# Revit family: PRD_AR_DrnngTps_DrainValve_ACXX2009
name_source: partatom
category: Plumbing Fixtures
units: mm (PartAtom-declared; Revit-internal decimal feet)

## family parameters
Always vertical = Yes
Cut with Voids When Loaded = No
OmniClass Number = 23.65.55.14.21
OmniClass Title = Non-Return Valves for Liquid Services
Part Type = Normal
Room Calculation Point = No
Round Connector Dimension = Use Diameter
Shared = No
Work Plane-Based = No

## types (1)
- ACXX2009
    AssetType = Fixed
    BIMObjectName = PRD_AR_DrainingTaps_DrainValve_ACXX2009
    BodyMaterial = PRD_AR_ChromatedBrass
    Category = Pr_65_54_95_27, Draining taps
    CloseOffRating = 0.0 Pa
    Default Elevation = 0 mm  [stored 0 ft]
    Description = Drain valve for automatic shower hose drainage for installation on wall-mounted mixers with hand shower connection, G 1/2 x G 1/2 A, polished chromium-plated brass.
    DurationUnit = year
    Features = for installation on wall-mounted mixers with hand shower connection
    FlowCoefficient = 0
    IfcExportAs = IfcValveType
    IfcExportType = USERDEFINED
    Manufacturer = KWC Group AG
    ManufacturerName = KWC Group AG
    ManufacturerURL = www.kwc.com
    Model = ACXX2009
    ModelNumber = 2030068123
    ModelReference = ACXX2009
    NBSDescription = Draining taps
    NBSReference = 90-10-90/374
    Name = Drain valve for automatic shower hose drainage ACXX2009
    NominalDepth = 0 mm  [stored 0 ft]
    NominalHeight = 0 mm  [stored 0 ft]
    NominalWidth = 0 mm  [stored 0 ft]
    ProductInformation = http://pim.kwc.com
    Quantity = 1
    QuantityUom = piece
    Size = 0.000000000000
    Status = New
    TailorMade = no
    TestPressure = 0.0 Pa
    URL = www.kwc.com
    Uniclass2015Code = Pr_65_54_95_27
    Uniclass2015Title = Draining taps
    Uniclass2015Version = Products v1.32
    ValveMechanism = OTHER
    ValveOperation = HYDRAULIC
    ValvePattern = ANGLED_2_PORT
    Version = 1
    WarrantyDurationUnit = year
    WorkingPressure = 0.0 Pa

note: [stored X ft] marks values corroborated as IEEE doubles in the binary element streams (Revit-internal decimal feet)

## geometry (parser evidence)
native form markers: Sweep x6
no freeform markers — native parametric forms only
